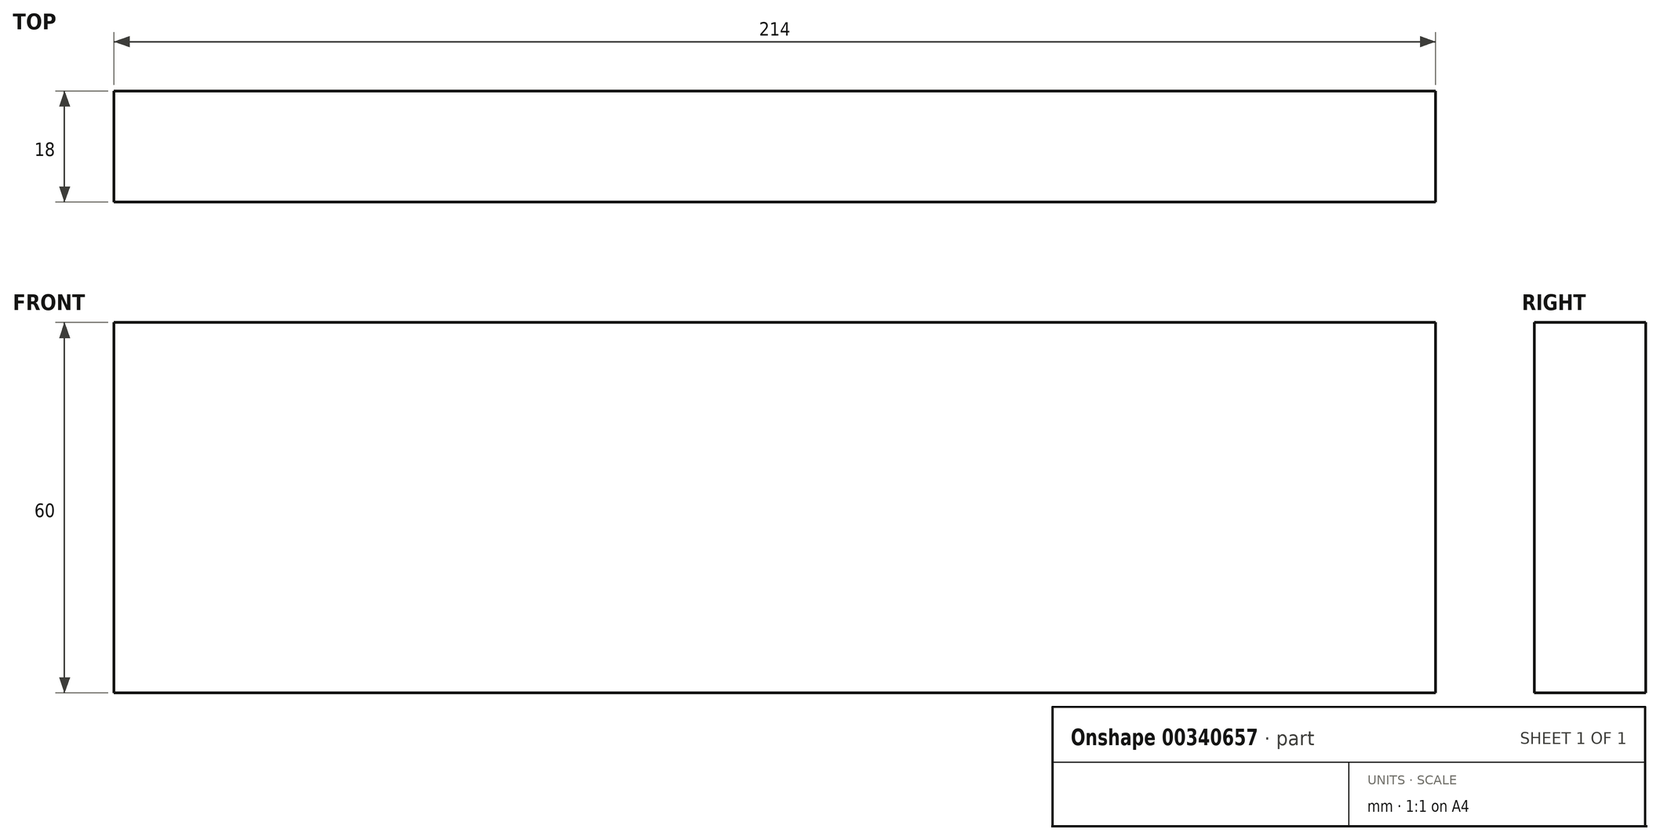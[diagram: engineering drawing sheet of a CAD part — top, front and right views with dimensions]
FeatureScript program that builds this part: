
annotation { "Feature Type Name" : "Feature", "Feature Type Description" : "" }
export const myFeature = defineFeature(function(context is Context, id is Id, definition is map)
    precondition{}
    {
        {
            var Q0;
            Q0=qCreatedBy(makeId("Front.planeOp"),FACE);
            var sketch = newSketch(context, id + "F0", { "sketchPlane" : qUnion([Q0])});
            skLineSegment(sketch, "E0.bottom", {"start": v(-65.24, 28.23) * mm, "end": v(148.76, 28.23) * mm});
            skLineSegment(sketch, "E0.top", {"start": v(-65.24, -31.77) * mm, "end": v(148.76, -31.77) * mm});
            skLineSegment(sketch, "E0.left", {"start": v(-65.24, 28.23) * mm, "end": v(-65.24, -31.77) * mm});
            skLineSegment(sketch, "E0.right", {"start": v(148.76, 28.23) * mm, "end": v(148.76, -31.77) * mm});
            skSolve(sketch);
        }
        {
            var Q0;
            Q0=makeQuery(id+"F0.imprint","IMPRINT",FACE,{"disambiguationData":[TD([[makeQuery(id+"F0.imprint","IMPRINT",EDGE,{"derivedFrom":sQuery(id+"F0.wireOp",EDGE,"E0.bottom")}),-1.0]])]});
            extrude(context, id + "F1", {"entities" : qUnion([Q0]), "depth" : 18 * mm});
        }
    });
